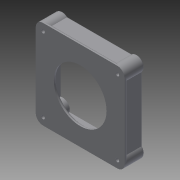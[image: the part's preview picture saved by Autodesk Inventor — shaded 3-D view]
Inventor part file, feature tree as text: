
AUTODESK INVENTOR PART (.ipt)
format: ipt  version: 2014 SP2 (Build 180246200, 246)  size: 215,552 bytes
history: native  units: mm
features: extrude x2, fillet x2, sketch x2
ambient origin geometry x8: Origin, YZ Plane, XZ Plane, XY Plane, X Axis, Y Axis, Z Axis, Center Point
bodies: Solid1 (feature_tree)
feature tree (6):
  extrude  "Extrusion1"  Depth=86.0mm
  extrude  "Extrusion2"  Depth=1.0mm
  fillet  "Fillet1"  Radius=43.0mm
  fillet  "Fillet2"  Radius=3.5mm
  sketch  "Sketch1"  dims[d0=51.0mm d1=86.0mm]
  sketch  "Sketch3"  dims[d2=86.0mm d3=43.0mm d4=43.0mm d9=3.5mm d11=3.5mm d12=3.5mm d13=3.0mm d14=0.0mm d20=7.0mm d25=3.5mm d26=7.0mm d27=7.0mm d29=7.0mm d30=7.0mm d31=7.0mm d32=7.0mm d33=7.0mm d34=7.0mm d35=72.0mm d36=5.0mm d37=5.0mm d38=5.0mm d39=5.0mm d40=76.0mm d41=76.0mm d42=3.0mm d43=3.0mm d44=3.0mm d45=3.0mm d46=16.0mm d47=0.0mm d48=2.0mm d49=1.0mm]
